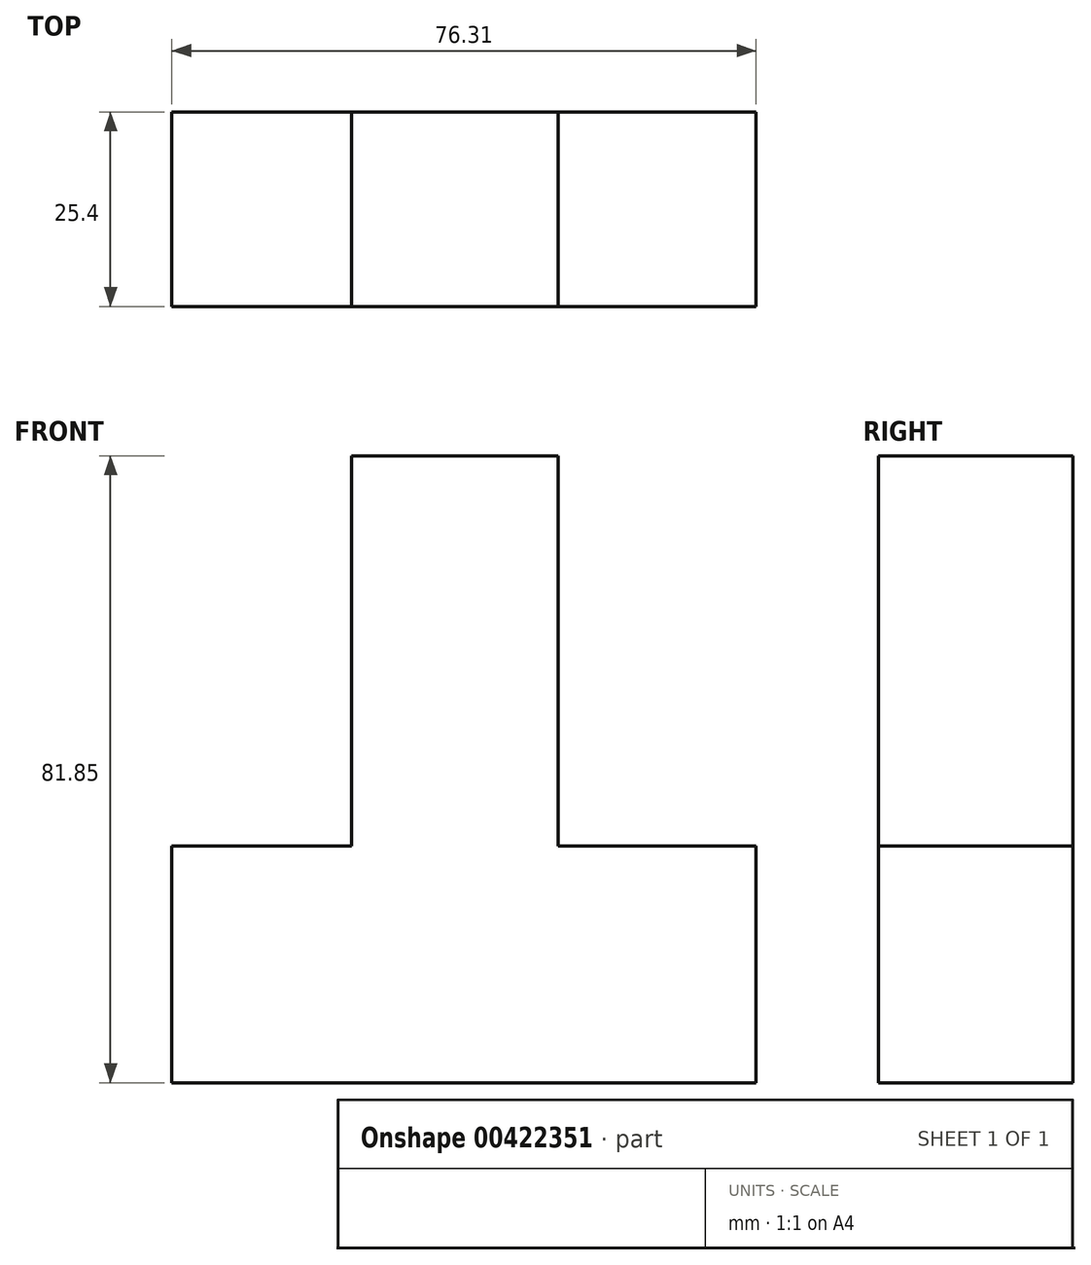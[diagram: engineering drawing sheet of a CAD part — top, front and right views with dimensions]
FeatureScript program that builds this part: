
annotation { "Feature Type Name" : "Feature", "Feature Type Description" : "" }
export const myFeature = defineFeature(function(context is Context, id is Id, definition is map)
    precondition{}
    {
        {
            var Q0;
            Q0=qCreatedBy(makeId("Front.planeOp"),FACE);
            var sketch = newSketch(context, id + "F0", { "sketchPlane" : qUnion([Q0])});
            skLineSegment(sketch, "E0", {"start": v(-28.78, 0) * mm, "end": v(-28.78, -30.9) * mm});
            skLineSegment(sketch, "E1", {"start": v(-28.78, -30.9) * mm, "end": v(47.53, -30.9) * mm});
            skLineSegment(sketch, "E2", {"start": v(47.53, -30.9) * mm, "end": v(47.53, 0) * mm});
            skLineSegment(sketch, "E3", {"start": v(47.53, 0) * mm, "end": v(21.65, 0) * mm});
            skLineSegment(sketch, "E4", {"start": v(21.65, 0) * mm, "end": v(21.65, 50.96) * mm});
            skLineSegment(sketch, "E5", {"start": v(21.65, 50.96) * mm, "end": v(-5.28, 50.96) * mm});
            skLineSegment(sketch, "E6", {"start": v(-5.28, 50.96) * mm, "end": v(-5.28, 0) * mm});
            skLineSegment(sketch, "E7", {"start": v(-5.28, 0) * mm, "end": v(-28.78, 0) * mm});
            skSolve(sketch);
        }
        {
            var Q0;
            Q0 = qSketchRegion(id + "F0", true);
            extrude(context, id + "F1", {"entities" : qUnion([Q0]), "depth" : 25.4 * mm});
        }
    });
